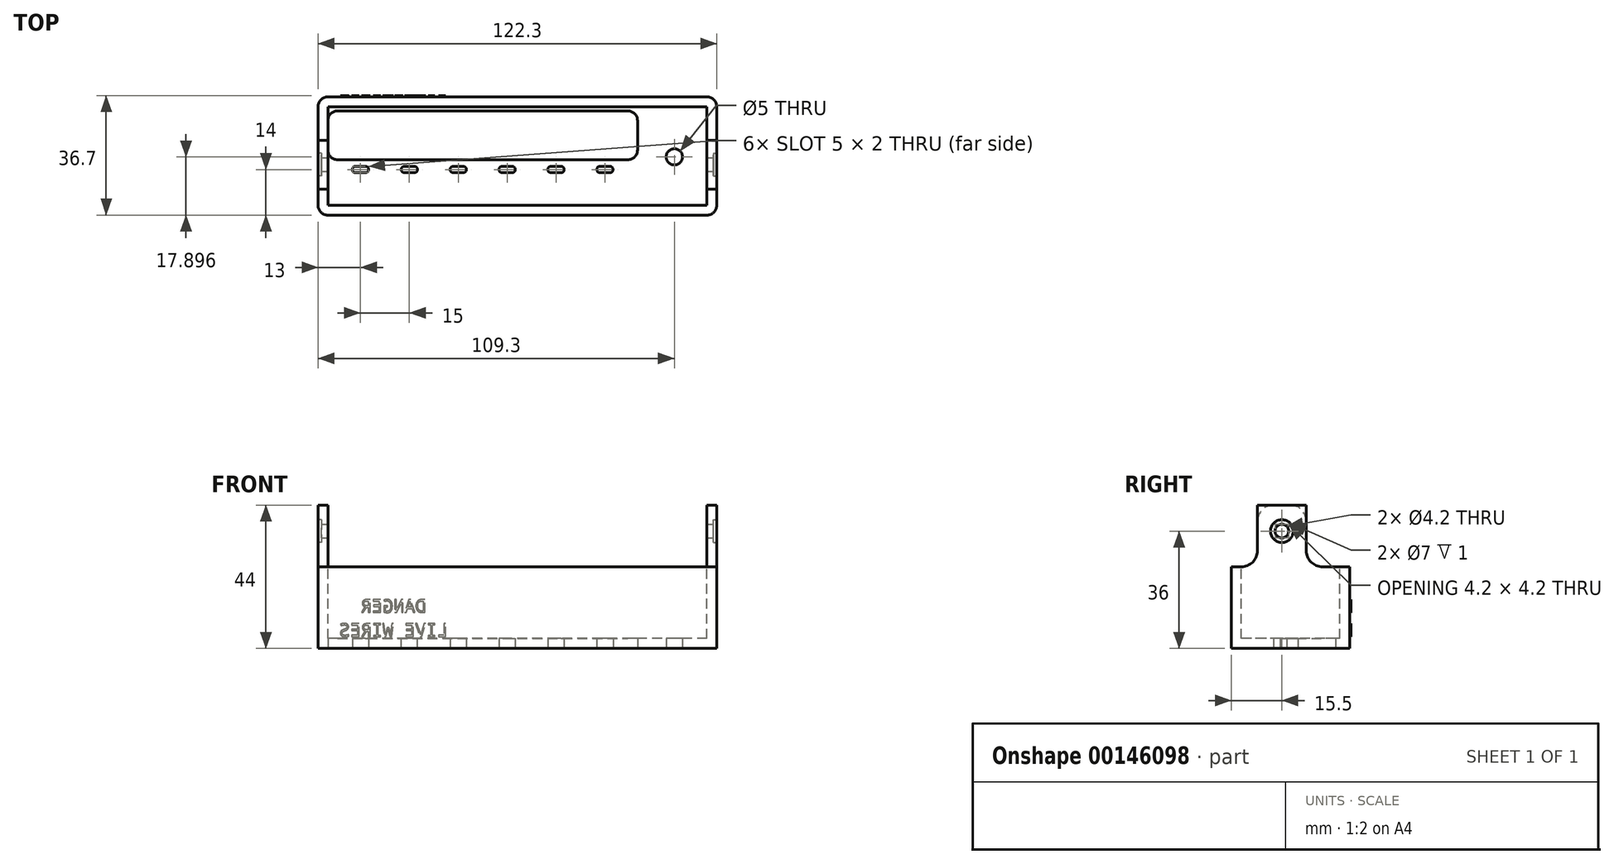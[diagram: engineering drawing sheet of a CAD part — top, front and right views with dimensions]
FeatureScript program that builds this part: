
annotation { "Feature Type Name" : "Feature", "Feature Type Description" : "" }
export const myFeature = defineFeature(function(context is Context, id is Id, definition is map)
    precondition{}
    {
        {
            var Q0;
            Q0=qCreatedBy(makeId("Top.planeOp"),FACE);
            var sketch = newSketch(context, id + "F0", { "sketchPlane" : qUnion([Q0])});
            skLineSegment(sketch, "E0.bottom", {"start": v(61.15, 18.15) * mm, "end": v(-61.15, 18.15) * mm});
            skLineSegment(sketch, "E0.top", {"start": v(61.15, -18.15) * mm, "end": v(-61.15, -18.15) * mm});
            skLineSegment(sketch, "E0.left", {"start": v(61.15, 18.15) * mm, "end": v(61.15, -18.15) * mm});
            skLineSegment(sketch, "E0.right", {"start": v(-61.15, 18.15) * mm, "end": v(-61.15, -18.15) * mm});
            skPoint(sketch, "E0.middle", {"position": v(0, 0) * mm});
            skSolve(sketch);
        }
        {
            var Q0;
            Q0=makeQuery(id+"F0.imprint","IMPRINT",FACE,{"disambiguationData":[TD([[makeQuery(id+"F0.imprint","IMPRINT",EDGE,{"derivedFrom":sQuery(id+"F0.wireOp",EDGE,"E0.bottom")}),1.0]])]});
            var Q1;
            Q1 = qSketchRegion(id + "F2", true);
            extrude(context, id + "F1", {"entities" : qUnion([Q0, Q1]), "depth" : 44 * mm});
        }
        {
            var Q0;
            Q0=makeQuery(id+"F1.opExtrude","CAP_FACE",FACE,{"disambiguationData":[OSD([sQuery(id+"F0.wireOp",EDGE,"E0.bottom"),sQuery(id+"F0.wireOp",EDGE,"E0.top"),sQuery(id+"F0.wireOp",EDGE,"E0.left"),sQuery(id+"F0.wireOp",EDGE,"E0.right")])],"isStart":false});
            var sketch = newSketch(context, id + "F2", { "sketchPlane" : qUnion([Q0])});
            skLineSegment(sketch, "E1.bottom", {"start": v(58.15, 15.15) * mm, "end": v(-58.15, 15.15) * mm});
            skLineSegment(sketch, "E1.top", {"start": v(58.15, -15.15) * mm, "end": v(-58.15, -15.15) * mm});
            skLineSegment(sketch, "E1.left", {"start": v(58.15, 15.15) * mm, "end": v(58.15, -15.15) * mm});
            skLineSegment(sketch, "E1.right", {"start": v(-58.15, 15.15) * mm, "end": v(-58.15, -15.15) * mm});
            skPoint(sketch, "E1.middle", {"position": v(0, 0) * mm});
            skSolve(sketch);
        }
        {
            var Q0;
            Q0=makeQuery(id+"F2.imprint","IMPRINT",FACE,{"disambiguationData":[TD([[makeQuery(id+"F2.imprint","IMPRINT",EDGE,{"derivedFrom":sQuery(id+"F2.wireOp",EDGE,"E1.bottom")}),1.0]])]});
            extrude(context, id + "F3", {"entities" : qUnion([Q0]), "operationType" : NewBodyOperationType.REMOVE, "oppositeDirection" : true, "depth" : 41 * mm});
        }
        {
            var Q0;
            Q0=makeQuery(id+"F1.opExtrude","SWEPT_FACE",FACE,{"disambiguationData":[OSD([sQuery(id+"F0.wireOp",EDGE,"E0.left")])]});
            var sketch = newSketch(context, id + "F4", { "sketchPlane" : qUnion([Q0])});
            skCircle(sketch, "E2", {"center": v(-2.65, 36) * mm, "radius": 2.1 * mm});
            skSolve(sketch);
        }
        {
            var Q0;
            Q0=makeQuery(id+"F4.imprint","IMPRINT",FACE,{"disambiguationData":[TD([[makeQuery(id+"F4.imprint","IMPRINT",EDGE,{"derivedFrom":sQuery(id+"F4.wireOp",EDGE,"E2")}),1.0]])]});
            extrude(context, id + "F5", {"entities" : qUnion([Q0]), "operationType" : NewBodyOperationType.REMOVE, "oppositeDirection" : true, "depth" : 500 * mm});
        }
        {
            var Q0;
            Q0=qCreatedBy(makeId("Top.planeOp"),FACE);
            var sketch = newSketch(context, id + "F6", { "sketchPlane" : qUnion([Q0])});
            skLineSegment(sketch, "E3.bottom", {"start": v(36.85, 13.85) * mm, "end": v(-58.15, 13.85) * mm});
            skLineSegment(sketch, "E3.top", {"start": v(36.85, -1.15) * mm, "end": v(-58.15, -1.15) * mm});
            skLineSegment(sketch, "E3.left", {"start": v(36.85, 13.85) * mm, "end": v(36.85, -1.15) * mm});
            skLineSegment(sketch, "E3.right", {"start": v(-58.15, 13.85) * mm, "end": v(-58.15, -1.15) * mm});
            skSolve(sketch);
        }
        {
            var Q0;
            Q0=makeQuery(id+"F6.imprint","IMPRINT",FACE,{"disambiguationData":[TD([[makeQuery(id+"F6.imprint","IMPRINT",EDGE,{"derivedFrom":sQuery(id+"F6.wireOp",EDGE,"E3.bottom")}),1.0]])]});
            extrude(context, id + "F7", {"entities" : qUnion([Q0]), "operationType" : NewBodyOperationType.REMOVE, "depth" : 25 * mm});
        }
        {
            var Q0;
            Q0=makeQuery(id+"F1.opExtrude","SWEPT_EDGE",EDGE,{"disambiguationData":[OSD([sQuery(id+"F0.wireOp",EDGE,"E0.top"),sQuery(id+"F0.wireOp",EDGE,"E0.right")])]});
            var Q1;
            Q1=makeQuery(id+"F1.opExtrude","SWEPT_EDGE",EDGE,{"disambiguationData":[OSD([sQuery(id+"F0.wireOp",EDGE,"E0.bottom"),sQuery(id+"F0.wireOp",EDGE,"E0.right")])]});
            var Q2;
            Q2=makeQuery(id+"F1.opExtrude","SWEPT_EDGE",EDGE,{"disambiguationData":[OSD([sQuery(id+"F0.wireOp",EDGE,"E0.bottom"),sQuery(id+"F0.wireOp",EDGE,"E0.left")])]});
            var Q3;
            Q3=makeQuery(id+"F1.opExtrude","SWEPT_EDGE",EDGE,{"disambiguationData":[OSD([sQuery(id+"F0.wireOp",EDGE,"E0.top"),sQuery(id+"F0.wireOp",EDGE,"E0.left")])]});
            var Q4;
            Q4=makeQuery(id+"F7.boolean.opBoolean","COPY",EDGE,{"derivedFrom":makeQuery(id+"F7.opExtrude","SWEPT_EDGE",EDGE,{"disambiguationData":[OSD([sQuery(id+"F6.wireOp",EDGE,"E3.bottom"),sQuery(id+"F6.wireOp",EDGE,"E3.left")])]})});
            var Q5;
            Q5=makeQuery(id+"F7.boolean.opBoolean","COPY",EDGE,{"derivedFrom":makeQuery(id+"F7.opExtrude","SWEPT_EDGE",EDGE,{"disambiguationData":[OSD([sQuery(id+"F6.wireOp",EDGE,"E3.bottom"),sQuery(id+"F6.wireOp",EDGE,"E3.right")])]})});
            var Q6;
            Q6=makeQuery(id+"F7.boolean.opBoolean","COPY",EDGE,{"derivedFrom":makeQuery(id+"F7.opExtrude","SWEPT_EDGE",EDGE,{"disambiguationData":[OSD([sQuery(id+"F6.wireOp",EDGE,"E3.top"),sQuery(id+"F6.wireOp",EDGE,"E3.right")])]})});
            var Q7;
            Q7=makeQuery(id+"F7.boolean.opBoolean","COPY",EDGE,{"derivedFrom":makeQuery(id+"F7.opExtrude","SWEPT_EDGE",EDGE,{"disambiguationData":[OSD([sQuery(id+"F6.wireOp",EDGE,"E3.top"),sQuery(id+"F6.wireOp",EDGE,"E3.left")])]})});
            fillet(context, id + "F8", {"entities" : qUnion([Q0, Q1, Q2, Q3, Q4, Q5, Q6, Q7]), "radius" : 3 * mm, "tangentPropagation" : true, "allowEdgeOverflow" : false});
        }
        {
            var Q0;
            Q0=qCreatedBy(makeId("Top.planeOp"),FACE);
            var sketch = newSketch(context, id + "F9", { "sketchPlane" : qUnion([Q0])});
            skLineSegment(sketch, "E4.bottom", {"start": v(-50.65, -5.15) * mm, "end": v(-45.65, -5.15) * mm});
            skLineSegment(sketch, "E4.top", {"start": v(-50.65, -3.15) * mm, "end": v(-45.65, -3.15) * mm});
            skLineSegment(sketch, "E4.left", {"start": v(-50.65, -5.15) * mm, "end": v(-50.65, -3.15) * mm});
            skLineSegment(sketch, "E4.right", {"start": v(-45.65, -5.15) * mm, "end": v(-45.65, -3.15) * mm});
            skLineSegment(sketch, "E5.bottom", {"start": v(-35.65, -5.15) * mm, "end": v(-30.65, -5.15) * mm});
            skLineSegment(sketch, "E5.top", {"start": v(-35.65, -3.15) * mm, "end": v(-30.65, -3.15) * mm});
            skLineSegment(sketch, "E5.left", {"start": v(-35.65, -5.15) * mm, "end": v(-35.65, -3.15) * mm});
            skLineSegment(sketch, "E5.right", {"start": v(-30.65, -5.15) * mm, "end": v(-30.65, -3.15) * mm});
            skLineSegment(sketch, "E6.bottom", {"start": v(-20.65, -5.15) * mm, "end": v(-15.65, -5.15) * mm});
            skLineSegment(sketch, "E6.top", {"start": v(-20.65, -3.15) * mm, "end": v(-15.65, -3.15) * mm});
            skLineSegment(sketch, "E6.left", {"start": v(-20.65, -5.15) * mm, "end": v(-20.65, -3.15) * mm});
            skLineSegment(sketch, "E6.right", {"start": v(-15.65, -5.15) * mm, "end": v(-15.65, -3.15) * mm});
            skLineSegment(sketch, "E7.bottom", {"start": v(-5.65, -5.15) * mm, "end": v(-0.65, -5.15) * mm});
            skLineSegment(sketch, "E7.top", {"start": v(-5.65, -3.15) * mm, "end": v(-0.65, -3.15) * mm});
            skLineSegment(sketch, "E7.left", {"start": v(-5.65, -5.15) * mm, "end": v(-5.65, -3.15) * mm});
            skLineSegment(sketch, "E7.right", {"start": v(-0.65, -5.15) * mm, "end": v(-0.65, -3.15) * mm});
            skLineSegment(sketch, "E8.bottom", {"start": v(9.35, -5.15) * mm, "end": v(14.35, -5.15) * mm});
            skLineSegment(sketch, "E8.top", {"start": v(9.35, -3.15) * mm, "end": v(14.35, -3.15) * mm});
            skLineSegment(sketch, "E8.left", {"start": v(9.35, -5.15) * mm, "end": v(9.35, -3.15) * mm});
            skLineSegment(sketch, "E8.right", {"start": v(14.35, -5.15) * mm, "end": v(14.35, -3.15) * mm});
            skLineSegment(sketch, "E9.bottom", {"start": v(24.35, -5.15) * mm, "end": v(29.35, -5.15) * mm});
            skLineSegment(sketch, "E9.top", {"start": v(24.35, -3.15) * mm, "end": v(29.35, -3.15) * mm});
            skLineSegment(sketch, "E9.left", {"start": v(24.35, -5.15) * mm, "end": v(24.35, -3.15) * mm});
            skLineSegment(sketch, "E9.right", {"start": v(29.35, -5.15) * mm, "end": v(29.35, -3.15) * mm});
            skLineSegment(sketch, "E10", {"start": v(48.15, -18.25) * mm, "end": v(48.15, -0.25) * mm, "construction": true});
            skCircle(sketch, "E11", {"center": v(48.15, -0.25) * mm, "radius": 2.5 * mm});
            skSolve(sketch);
        }
        {
            var Q0;
            Q0=makeQuery(id+"F9.imprint","IMPRINT",FACE,{"disambiguationData":[TD([[makeQuery(id+"F9.imprint","IMPRINT",EDGE,{"derivedFrom":sQuery(id+"F9.wireOp",EDGE,"E11")}),1.0]])]});
            var Q1;
            Q1=makeQuery(id+"F9.imprint","IMPRINT",FACE,{"disambiguationData":[TD([[makeQuery(id+"F9.imprint","IMPRINT",EDGE,{"derivedFrom":sQuery(id+"F9.wireOp",EDGE,"E9.bottom")}),1.0]])]});
            var Q2;
            Q2=makeQuery(id+"F9.imprint","IMPRINT",FACE,{"disambiguationData":[TD([[makeQuery(id+"F9.imprint","IMPRINT",EDGE,{"derivedFrom":sQuery(id+"F9.wireOp",EDGE,"E8.bottom")}),1.0]])]});
            var Q3;
            Q3=makeQuery(id+"F9.imprint","IMPRINT",FACE,{"disambiguationData":[TD([[makeQuery(id+"F9.imprint","IMPRINT",EDGE,{"derivedFrom":sQuery(id+"F9.wireOp",EDGE,"E7.bottom")}),1.0]])]});
            var Q4;
            Q4=makeQuery(id+"F9.imprint","IMPRINT",FACE,{"disambiguationData":[TD([[makeQuery(id+"F9.imprint","IMPRINT",EDGE,{"derivedFrom":sQuery(id+"F9.wireOp",EDGE,"E6.bottom")}),1.0]])]});
            var Q5;
            Q5=makeQuery(id+"F9.imprint","IMPRINT",FACE,{"disambiguationData":[TD([[makeQuery(id+"F9.imprint","IMPRINT",EDGE,{"derivedFrom":sQuery(id+"F9.wireOp",EDGE,"E5.bottom")}),1.0]])]});
            var Q6;
            Q6=makeQuery(id+"F9.imprint","IMPRINT",FACE,{"disambiguationData":[TD([[makeQuery(id+"F9.imprint","IMPRINT",EDGE,{"derivedFrom":sQuery(id+"F9.wireOp",EDGE,"E4.bottom")}),1.0]])]});
            extrude(context, id + "F10", {"entities" : qUnion([Q0, Q1, Q2, Q3, Q4, Q5, Q6]), "operationType" : NewBodyOperationType.REMOVE, "depth" : 25 * mm});
        }
        {
            var Q0;
            Q0=makeQuery(id+"F10.boolean.opBoolean","COPY",EDGE,{"derivedFrom":makeQuery(id+"F10.opExtrude","SWEPT_EDGE",EDGE,{"disambiguationData":[OSD([sQuery(id+"F9.wireOp",EDGE,"E4.bottom"),sQuery(id+"F9.wireOp",EDGE,"E4.left")])]})});
            var Q1;
            Q1=makeQuery(id+"F10.boolean.opBoolean","COPY",EDGE,{"derivedFrom":makeQuery(id+"F10.opExtrude","SWEPT_EDGE",EDGE,{"disambiguationData":[OSD([sQuery(id+"F9.wireOp",EDGE,"E4.top"),sQuery(id+"F9.wireOp",EDGE,"E4.left")])]})});
            var Q2;
            Q2=makeQuery(id+"F10.boolean.opBoolean","COPY",EDGE,{"derivedFrom":makeQuery(id+"F10.opExtrude","SWEPT_EDGE",EDGE,{"disambiguationData":[OSD([sQuery(id+"F9.wireOp",EDGE,"E4.top"),sQuery(id+"F9.wireOp",EDGE,"E4.right")])]})});
            var Q3;
            Q3=makeQuery(id+"F10.boolean.opBoolean","COPY",EDGE,{"derivedFrom":makeQuery(id+"F10.opExtrude","SWEPT_EDGE",EDGE,{"disambiguationData":[OSD([sQuery(id+"F9.wireOp",EDGE,"E4.bottom"),sQuery(id+"F9.wireOp",EDGE,"E4.right")])]})});
            var Q4;
            Q4=makeQuery(id+"F10.boolean.opBoolean","COPY",EDGE,{"derivedFrom":makeQuery(id+"F10.opExtrude","SWEPT_EDGE",EDGE,{"disambiguationData":[OSD([sQuery(id+"F9.wireOp",EDGE,"E5.bottom"),sQuery(id+"F9.wireOp",EDGE,"E5.right")])]})});
            var Q5;
            Q5=makeQuery(id+"F10.boolean.opBoolean","COPY",EDGE,{"derivedFrom":makeQuery(id+"F10.opExtrude","SWEPT_EDGE",EDGE,{"disambiguationData":[OSD([sQuery(id+"F9.wireOp",EDGE,"E5.top"),sQuery(id+"F9.wireOp",EDGE,"E5.right")])]})});
            var Q6;
            Q6=makeQuery(id+"F10.boolean.opBoolean","COPY",EDGE,{"derivedFrom":makeQuery(id+"F10.opExtrude","SWEPT_EDGE",EDGE,{"disambiguationData":[OSD([sQuery(id+"F9.wireOp",EDGE,"E5.top"),sQuery(id+"F9.wireOp",EDGE,"E5.left")])]})});
            var Q7;
            Q7=makeQuery(id+"F10.boolean.opBoolean","COPY",EDGE,{"derivedFrom":makeQuery(id+"F10.opExtrude","SWEPT_EDGE",EDGE,{"disambiguationData":[OSD([sQuery(id+"F9.wireOp",EDGE,"E5.bottom"),sQuery(id+"F9.wireOp",EDGE,"E5.left")])]})});
            var Q8;
            Q8=makeQuery(id+"F10.boolean.opBoolean","COPY",EDGE,{"derivedFrom":makeQuery(id+"F10.opExtrude","SWEPT_EDGE",EDGE,{"disambiguationData":[OSD([sQuery(id+"F9.wireOp",EDGE,"E6.bottom"),sQuery(id+"F9.wireOp",EDGE,"E6.left")])]})});
            var Q9;
            Q9=makeQuery(id+"F10.boolean.opBoolean","COPY",EDGE,{"derivedFrom":makeQuery(id+"F10.opExtrude","SWEPT_EDGE",EDGE,{"disambiguationData":[OSD([sQuery(id+"F9.wireOp",EDGE,"E7.bottom"),sQuery(id+"F9.wireOp",EDGE,"E7.left")])]})});
            var Q10;
            Q10=makeQuery(id+"F10.boolean.opBoolean","COPY",EDGE,{"derivedFrom":makeQuery(id+"F10.opExtrude","SWEPT_EDGE",EDGE,{"disambiguationData":[OSD([sQuery(id+"F9.wireOp",EDGE,"E8.bottom"),sQuery(id+"F9.wireOp",EDGE,"E8.left")])]})});
            var Q11;
            Q11=makeQuery(id+"F10.boolean.opBoolean","COPY",EDGE,{"derivedFrom":makeQuery(id+"F10.opExtrude","SWEPT_EDGE",EDGE,{"disambiguationData":[OSD([sQuery(id+"F9.wireOp",EDGE,"E9.bottom"),sQuery(id+"F9.wireOp",EDGE,"E9.left")])]})});
            var Q12;
            Q12=makeQuery(id+"F10.boolean.opBoolean","COPY",EDGE,{"derivedFrom":makeQuery(id+"F10.opExtrude","SWEPT_EDGE",EDGE,{"disambiguationData":[OSD([sQuery(id+"F9.wireOp",EDGE,"E9.top"),sQuery(id+"F9.wireOp",EDGE,"E9.right")])]})});
            var Q13;
            Q13=makeQuery(id+"F10.boolean.opBoolean","COPY",EDGE,{"derivedFrom":makeQuery(id+"F10.opExtrude","SWEPT_EDGE",EDGE,{"disambiguationData":[OSD([sQuery(id+"F9.wireOp",EDGE,"E8.top"),sQuery(id+"F9.wireOp",EDGE,"E8.right")])]})});
            var Q14;
            Q14=makeQuery(id+"F10.boolean.opBoolean","COPY",EDGE,{"derivedFrom":makeQuery(id+"F10.opExtrude","SWEPT_EDGE",EDGE,{"disambiguationData":[OSD([sQuery(id+"F9.wireOp",EDGE,"E7.top"),sQuery(id+"F9.wireOp",EDGE,"E7.right")])]})});
            var Q15;
            Q15=makeQuery(id+"F10.boolean.opBoolean","COPY",EDGE,{"derivedFrom":makeQuery(id+"F10.opExtrude","SWEPT_EDGE",EDGE,{"disambiguationData":[OSD([sQuery(id+"F9.wireOp",EDGE,"E6.top"),sQuery(id+"F9.wireOp",EDGE,"E6.right")])]})});
            var Q16;
            Q16=makeQuery(id+"F10.boolean.opBoolean","COPY",EDGE,{"derivedFrom":makeQuery(id+"F10.opExtrude","SWEPT_EDGE",EDGE,{"disambiguationData":[OSD([sQuery(id+"F9.wireOp",EDGE,"E6.top"),sQuery(id+"F9.wireOp",EDGE,"E6.left")])]})});
            var Q17;
            Q17=makeQuery(id+"F10.boolean.opBoolean","COPY",EDGE,{"derivedFrom":makeQuery(id+"F10.opExtrude","SWEPT_EDGE",EDGE,{"disambiguationData":[OSD([sQuery(id+"F9.wireOp",EDGE,"E7.top"),sQuery(id+"F9.wireOp",EDGE,"E7.left")])]})});
            var Q18;
            Q18=makeQuery(id+"F10.boolean.opBoolean","COPY",EDGE,{"derivedFrom":makeQuery(id+"F10.opExtrude","SWEPT_EDGE",EDGE,{"disambiguationData":[OSD([sQuery(id+"F9.wireOp",EDGE,"E8.top"),sQuery(id+"F9.wireOp",EDGE,"E8.left")])]})});
            var Q19;
            Q19=makeQuery(id+"F10.boolean.opBoolean","COPY",EDGE,{"derivedFrom":makeQuery(id+"F10.opExtrude","SWEPT_EDGE",EDGE,{"disambiguationData":[OSD([sQuery(id+"F9.wireOp",EDGE,"E9.top"),sQuery(id+"F9.wireOp",EDGE,"E9.left")])]})});
            var Q20;
            Q20=makeQuery(id+"F10.boolean.opBoolean","COPY",EDGE,{"derivedFrom":makeQuery(id+"F10.opExtrude","SWEPT_EDGE",EDGE,{"disambiguationData":[OSD([sQuery(id+"F9.wireOp",EDGE,"E9.bottom"),sQuery(id+"F9.wireOp",EDGE,"E9.right")])]})});
            var Q21;
            Q21=makeQuery(id+"F10.boolean.opBoolean","COPY",EDGE,{"derivedFrom":makeQuery(id+"F10.opExtrude","SWEPT_EDGE",EDGE,{"disambiguationData":[OSD([sQuery(id+"F9.wireOp",EDGE,"E8.bottom"),sQuery(id+"F9.wireOp",EDGE,"E8.right")])]})});
            var Q22;
            Q22=makeQuery(id+"F10.boolean.opBoolean","COPY",EDGE,{"derivedFrom":makeQuery(id+"F10.opExtrude","SWEPT_EDGE",EDGE,{"disambiguationData":[OSD([sQuery(id+"F9.wireOp",EDGE,"E7.bottom"),sQuery(id+"F9.wireOp",EDGE,"E7.right")])]})});
            var Q23;
            Q23=makeQuery(id+"F10.boolean.opBoolean","COPY",EDGE,{"derivedFrom":makeQuery(id+"F10.opExtrude","SWEPT_EDGE",EDGE,{"disambiguationData":[OSD([sQuery(id+"F9.wireOp",EDGE,"E6.bottom"),sQuery(id+"F9.wireOp",EDGE,"E6.right")])]})});
            fillet(context, id + "F11", {"entities" : qUnion([Q0, Q1, Q2, Q3, Q4, Q5, Q6, Q7, Q8, Q9, Q10, Q11, Q12, Q13, Q14, Q15, Q16, Q17, Q18, Q19, Q20, Q21, Q22, Q23]), "radius" : 1 * mm, "tangentPropagation" : true, "allowEdgeOverflow" : false});
        }
        {
            var Q0;
            Q0=makeQuery(id+"F1.opExtrude","SWEPT_FACE",FACE,{"disambiguationData":[OSD([sQuery(id+"F0.wireOp",EDGE,"E0.left")])]});
            var sketch = newSketch(context, id + "F12", { "sketchPlane" : qUnion([Q0])});
            skCircle(sketch, "E12", {"center": v(-2.65, 36) * mm, "radius": 3.5 * mm});
            skSolve(sketch);
        }
        {
            var Q0;
            Q0=makeQuery(id+"F12.imprint","IMPRINT",FACE,{"disambiguationData":[TD([[makeQuery(id+"F12.imprint","IMPRINT",EDGE,{"derivedFrom":sQuery(id+"F12.wireOp",EDGE,"E12")}),1.0]])]});
            extrude(context, id + "F13", {"entities" : qUnion([Q0]), "operationType" : NewBodyOperationType.REMOVE, "oppositeDirection" : true, "depth" : 1 * mm});
        }
        {
            var Q0;
            Q0=makeQuery(id+"F1.opExtrude","SWEPT_FACE",FACE,{"disambiguationData":[OSD([sQuery(id+"F0.wireOp",EDGE,"E0.right")])]});
            var sketch = newSketch(context, id + "F14", { "sketchPlane" : qUnion([Q0])});
            skCircle(sketch, "E13", {"center": v(2.65, 36) * mm, "radius": 3.5 * mm});
            skSolve(sketch);
        }
        {
            var Q0;
            Q0=makeQuery(id+"F14.imprint","IMPRINT",FACE,{"disambiguationData":[TD([[makeQuery(id+"F14.imprint","IMPRINT",EDGE,{"derivedFrom":sQuery(id+"F14.wireOp",EDGE,"E13")}),1.0]])]});
            extrude(context, id + "F15", {"entities" : qUnion([Q0]), "operationType" : NewBodyOperationType.REMOVE, "oppositeDirection" : true, "depth" : 1 * mm});
        }
        {
            var Q0;
            Q0=makeQuery(id+"F1.opExtrude","SWEPT_FACE",FACE,{"disambiguationData":[OSD([sQuery(id+"F0.wireOp",EDGE,"E0.left")])]});
            var sketch = newSketch(context, id + "F16", { "sketchPlane" : qUnion([Q0])});
            skLineSegment(sketch, "E14.bottom", {"start": v(4.85, 44) * mm, "end": v(19.3, 44) * mm});
            skLineSegment(sketch, "E14.top", {"start": v(4.85, 25) * mm, "end": v(19.3, 25) * mm});
            skLineSegment(sketch, "E14.left", {"start": v(4.85, 44) * mm, "end": v(4.85, 25) * mm});
            skLineSegment(sketch, "E14.right", {"start": v(19.3, 44) * mm, "end": v(19.3, 25) * mm});
            skPoint(sketch, "E15.oppositeSnap0", {"position": v(-15.15, 21) * mm});
            skLineSegment(sketch, "E16.bottom", {"start": v(-10.15, 44) * mm, "end": v(-20.8, 44) * mm});
            skLineSegment(sketch, "E16.top", {"start": v(-10.15, 25) * mm, "end": v(-20.8, 25) * mm});
            skLineSegment(sketch, "E16.left", {"start": v(-10.15, 44) * mm, "end": v(-10.15, 25) * mm});
            skLineSegment(sketch, "E16.right", {"start": v(-20.8, 44) * mm, "end": v(-20.8, 25) * mm});
            skSolve(sketch);
        }
        {
            var Q0;
            {var subQ4=sQuery(id+"F16.wireOp",EDGE,"E15.right");Q0=makeQuery(id+"F16.imprint","IMPRINT",FACE,{"disambiguationData":[TD([[makeQuery(id+"F16.imprint","IMPRINT",EDGE,{"derivedFrom":subQ4}),1.0]])]});}
            var Q1;
            {var subQ4=sQuery(id+"F16.wireOp",EDGE,"E15.left");Q1=makeQuery(id+"F16.imprint","IMPRINT",FACE,{"disambiguationData":[TD([[makeQuery(id+"F16.imprint","IMPRINT",EDGE,{"derivedFrom":subQ4}),-1.0]])]});}
            var Q2;
            {var subQ4=sQuery(id+"F16.wireOp",EDGE,"E14.left");Q2=makeQuery(id+"F16.imprint","IMPRINT",FACE,{"disambiguationData":[TD([[makeQuery(id+"F16.imprint","IMPRINT",EDGE,{"derivedFrom":subQ4}),1.0]])]});}
            var Q3;
            {var subQ4=sQuery(id+"F16.wireOp",EDGE,"E14.right");Q3=makeQuery(id+"F16.imprint","IMPRINT",FACE,{"disambiguationData":[TD([[makeQuery(id+"F16.imprint","IMPRINT",EDGE,{"derivedFrom":subQ4}),-1.0]])]});}
            var Q4;
            {var subQ4=sQuery(id+"F16.wireOp",EDGE,"E16.right");Q4=makeQuery(id+"F16.imprint","IMPRINT",FACE,{"disambiguationData":[TD([[makeQuery(id+"F16.imprint","IMPRINT",EDGE,{"derivedFrom":subQ4}),1.0]])]});}
            var Q5;
            {var subQ4=sQuery(id+"F16.wireOp",EDGE,"E16.left");Q5=makeQuery(id+"F16.imprint","IMPRINT",FACE,{"disambiguationData":[TD([[makeQuery(id+"F16.imprint","IMPRINT",EDGE,{"derivedFrom":subQ4}),-1.0]])]});}
            extrude(context, id + "F17", {"entities" : qUnion([Q0, Q1, Q2, Q3, Q4, Q5]), "operationType" : NewBodyOperationType.REMOVE, "oppositeDirection" : true, "depth" : 200 * mm});
        }
        {
            var Q0;
            {var subQ0=sQuery(id+"F0.wireOp",EDGE,"E0.left");var subQ1=sQuery(id+"F16.wireOp",EDGE,"E15.left");Q0=makeQuery(id+"F17.boolean.opBoolean","COPY",EDGE,{"disambiguationData":[TD([makeQuery(id+"F1.opExtrude","SWEPT_FACE",FACE,{"disambiguationData":[OSD([subQ0])]})])],"derivedFrom":makeQuery(id+"F17.opExtrude","SWEPT_EDGE",EDGE,{"disambiguationData":[OSD([subQ0,sQuery(id+"F16.wireOp",EDGE,"E15.bottom"),subQ1])]})});}
            var Q1;
            {var subQ0=sQuery(id+"F0.wireOp",EDGE,"E0.left");var subQ1=sQuery(id+"F16.wireOp",EDGE,"E14.left");Q1=makeQuery(id+"F17.boolean.opBoolean","COPY",EDGE,{"disambiguationData":[TD([makeQuery(id+"F1.opExtrude","SWEPT_FACE",FACE,{"disambiguationData":[OSD([subQ0])]})])],"derivedFrom":makeQuery(id+"F17.opExtrude","SWEPT_EDGE",EDGE,{"disambiguationData":[OSD([subQ0,sQuery(id+"F16.wireOp",EDGE,"E14.bottom"),subQ1])]})});}
            var Q2;
            {var subQ0=sQuery(id+"F16.wireOp",EDGE,"E14.left");var subQ1=sQuery(id+"F0.wireOp",EDGE,"E0.right");var subQ2=sQuery(id+"F0.wireOp",EDGE,"E0.left");Q2=makeQuery(id+"F17.boolean.opBoolean","COPY",EDGE,{"disambiguationData":[TD([makeQuery(id+"F1.opExtrude","SWEPT_FACE",FACE,{"disambiguationData":[OSD([subQ1])]})])],"derivedFrom":makeQuery(id+"F17.opExtrude","SWEPT_EDGE",EDGE,{"disambiguationData":[OSD([subQ2,sQuery(id+"F16.wireOp",EDGE,"E14.bottom"),subQ0])]})});}
            var Q3;
            {var subQ0=sQuery(id+"F0.wireOp",EDGE,"E0.right");var subQ1=sQuery(id+"F0.wireOp",EDGE,"E0.left");var subQ2=sQuery(id+"F16.wireOp",EDGE,"E15.left");Q3=makeQuery(id+"F17.boolean.opBoolean","COPY",EDGE,{"disambiguationData":[TD([makeQuery(id+"F1.opExtrude","SWEPT_FACE",FACE,{"disambiguationData":[OSD([subQ0])]})])],"derivedFrom":makeQuery(id+"F17.opExtrude","SWEPT_EDGE",EDGE,{"disambiguationData":[OSD([subQ1,sQuery(id+"F16.wireOp",EDGE,"E15.bottom"),subQ2])]})});}
            fillet(context, id + "F18", {"entities" : qUnion([Q0, Q1, Q2, Q3]), "radius" : 5 * mm, "tangentPropagation" : true, "allowEdgeOverflow" : false});
        }
        {
            var Q0;
            {var subQ0=sQuery(id+"F16.wireOp",EDGE,"E15.left");var subQ1=sQuery(id+"F16.wireOp",EDGE,"E15.top");Q0=makeQuery(id+"F17.boolean.opBoolean","COPY",EDGE,{"disambiguationData":[TD([makeQuery(id+"F1.opExtrude","SWEPT_FACE",FACE,{"disambiguationData":[OSD([sQuery(id+"F0.wireOp",EDGE,"E0.left")])]})])],"derivedFrom":makeQuery(id+"F17.opExtrude","SWEPT_EDGE",EDGE,{"disambiguationData":[OSD([subQ1,subQ0])]})});}
            var Q1;
            {var subQ0=sQuery(id+"F16.wireOp",EDGE,"E14.top");var subQ1=sQuery(id+"F16.wireOp",EDGE,"E14.left");Q1=makeQuery(id+"F17.boolean.opBoolean","COPY",EDGE,{"disambiguationData":[TD([makeQuery(id+"F1.opExtrude","SWEPT_FACE",FACE,{"disambiguationData":[OSD([sQuery(id+"F0.wireOp",EDGE,"E0.left")])]})])],"derivedFrom":makeQuery(id+"F17.opExtrude","SWEPT_EDGE",EDGE,{"disambiguationData":[OSD([subQ0,subQ1])]})});}
            var Q2;
            {var subQ0=sQuery(id+"F16.wireOp",EDGE,"E15.top");var subQ1=sQuery(id+"F16.wireOp",EDGE,"E15.left");Q2=makeQuery(id+"F17.boolean.opBoolean","COPY",EDGE,{"disambiguationData":[TD([makeQuery(id+"F1.opExtrude","SWEPT_FACE",FACE,{"disambiguationData":[OSD([sQuery(id+"F0.wireOp",EDGE,"E0.right")])]})])],"derivedFrom":makeQuery(id+"F17.opExtrude","SWEPT_EDGE",EDGE,{"disambiguationData":[OSD([subQ0,subQ1])]})});}
            var Q3;
            {var subQ0=sQuery(id+"F16.wireOp",EDGE,"E14.top");var subQ1=sQuery(id+"F16.wireOp",EDGE,"E14.left");Q3=makeQuery(id+"F17.boolean.opBoolean","COPY",EDGE,{"disambiguationData":[TD([makeQuery(id+"F1.opExtrude","SWEPT_FACE",FACE,{"disambiguationData":[OSD([sQuery(id+"F0.wireOp",EDGE,"E0.right")])]})])],"derivedFrom":makeQuery(id+"F17.opExtrude","SWEPT_EDGE",EDGE,{"disambiguationData":[OSD([subQ0,subQ1])]})});}
            var Q4;
            {var subQ0=sQuery(id+"F16.wireOp",EDGE,"E16.left");var subQ1=sQuery(id+"F16.wireOp",EDGE,"E16.top");Q4=makeQuery(id+"F17.boolean.opBoolean","COPY",EDGE,{"disambiguationData":[TD([makeQuery(id+"F1.opExtrude","SWEPT_FACE",FACE,{"disambiguationData":[OSD([sQuery(id+"F0.wireOp",EDGE,"E0.left")])]})])],"derivedFrom":makeQuery(id+"F17.opExtrude","SWEPT_EDGE",EDGE,{"disambiguationData":[OSD([subQ1,subQ0])]})});}
            var Q5;
            {var subQ0=sQuery(id+"F16.wireOp",EDGE,"E16.top");var subQ1=sQuery(id+"F16.wireOp",EDGE,"E16.left");Q5=makeQuery(id+"F17.boolean.opBoolean","COPY",EDGE,{"disambiguationData":[TD([makeQuery(id+"F1.opExtrude","SWEPT_FACE",FACE,{"disambiguationData":[OSD([sQuery(id+"F0.wireOp",EDGE,"E0.right")])]})])],"derivedFrom":makeQuery(id+"F17.opExtrude","SWEPT_EDGE",EDGE,{"disambiguationData":[OSD([subQ0,subQ1])]})});}
            fillet(context, id + "F19", {"entities" : qUnion([Q0, Q1, Q2, Q3, Q4, Q5]), "radius" : 5 * mm, "tangentPropagation" : true, "allowEdgeOverflow" : false});
        }
        {
            var Q0;
            Q0=makeQuery(id+"F1.opExtrude","SWEPT_FACE",FACE,{"disambiguationData":[OSD([sQuery(id+"F0.wireOp",EDGE,"E0.bottom")])]});
            var sketch = newSketch(context, id + "F20", { "sketchPlane" : qUnion([Q0])});
            skText(sketch, "E17", { "text": "  DANGER\nLIVE WIRES", "fontName": "DroidSansMono.ttf"});
            const initialGuessF20  = {"E17": [0.02136, 0.011, 1, 0, 0.004]};
            skSetInitialGuess(sketch, initialGuessF20);
            skSolve(sketch);
        }
        {
            var Q0;
            Q0 = qSketchRegion(id + "F20", true);
            extrude(context, id + "F21", {"entities" : qUnion([Q0]), "operationType" : NewBodyOperationType.ADD, "depth" : .4 * mm});
        }
    });
